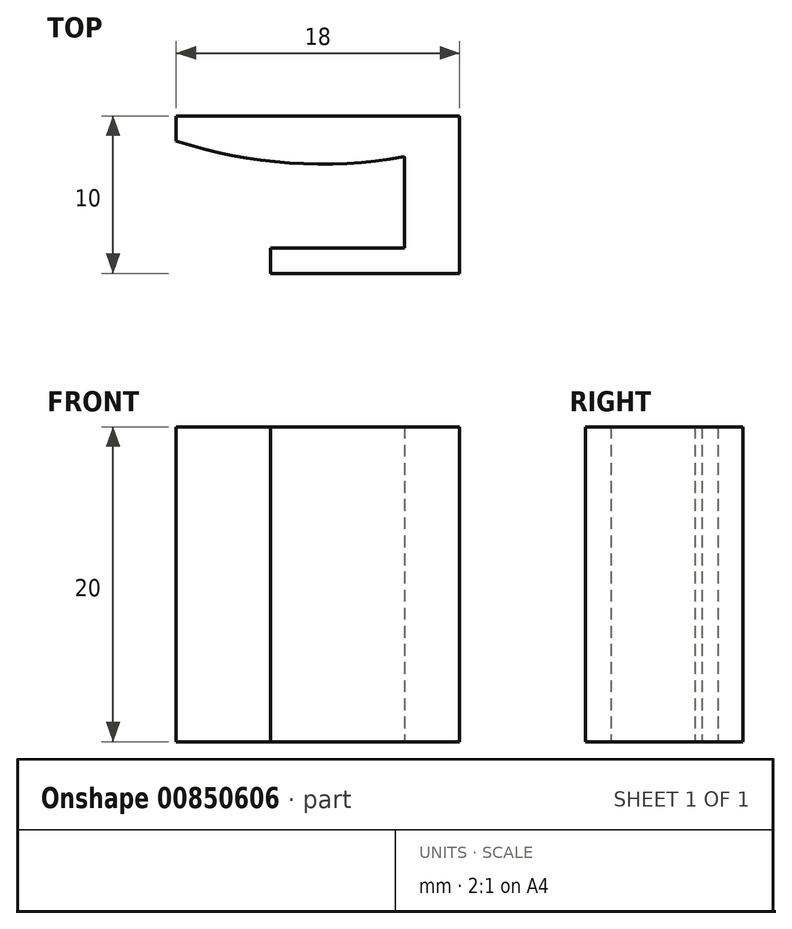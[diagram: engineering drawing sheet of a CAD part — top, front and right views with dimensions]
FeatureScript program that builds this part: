
annotation { "Feature Type Name" : "Feature", "Feature Type Description" : "" }
export const myFeature = defineFeature(function(context is Context, id is Id, definition is map)
    precondition{}
    {
        {
            var Q0;
            Q0=qCreatedBy(makeId("Top.planeOp"),FACE);
            var sketch = newSketch(context, id + "F0", { "sketchPlane" : qUnion([Q0])});
            skLineSegment(sketch, "E0", {"start": v(-12, 0) * mm, "end": v(0, 0) * mm});
            skLineSegment(sketch, "E1", {"start": v(0, 0) * mm, "end": v(0, 10) * mm});
            skLineSegment(sketch, "E2", {"start": v(0, 10) * mm, "end": v(-18, 10) * mm});
            skLineSegment(sketch, "E3", {"start": v(-18, 10) * mm, "end": v(-18, 8.4) * mm});
            skLineSegment(sketch, "E4", {"start": v(-3.5, 7.4) * mm, "end": v(-3.5, 1.6) * mm});
            skLineSegment(sketch, "E5", {"start": v(-3.5, 1.6) * mm, "end": v(-12, 1.6) * mm});
            skLineSegment(sketch, "E6", {"start": v(-12, 1.6) * mm, "end": v(-12, 0) * mm});
            skArc(sketch, "E7", {"start": v(-18, 8.4) * mm, "mid": v(-10.81, 7) * mm, "end": v(-3.5, 7.4) * mm});
            skSolve(sketch);
        }
        {
            var Q0;
            Q0=makeQuery(id+"F0.imprint","IMPRINT",FACE,{"disambiguationData":[TD([[makeQuery(id+"F0.imprint","IMPRINT",EDGE,{"derivedFrom":sQuery(id+"F0.wireOp",EDGE,"E0")}),1.0]])]});
            extrude(context, id + "F1", {"entities" : qUnion([Q0]), "depth" : 20 * mm, "offsetDistance" : 25 * mm});
        }
    });
